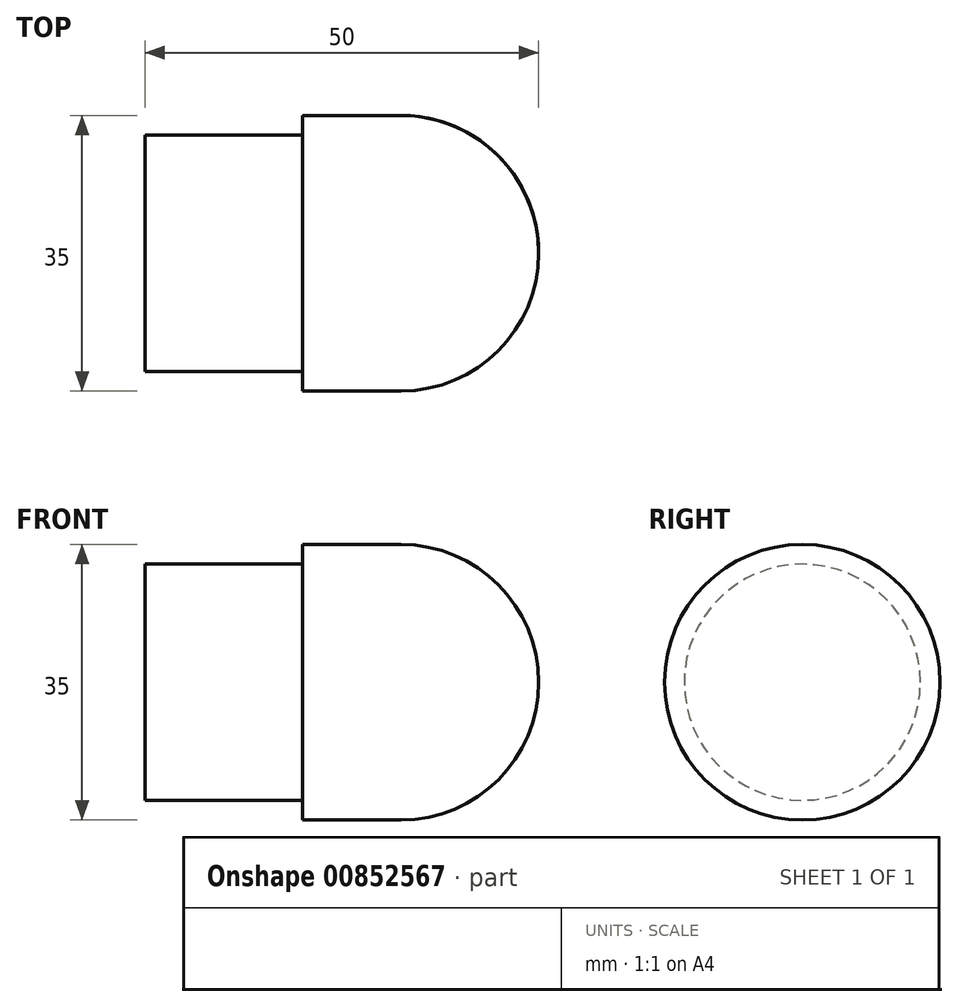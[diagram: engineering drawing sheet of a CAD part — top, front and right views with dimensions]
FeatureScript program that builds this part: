
annotation { "Feature Type Name" : "Feature", "Feature Type Description" : "" }
export const myFeature = defineFeature(function(context is Context, id is Id, definition is map)
    precondition{}
    {
        {
            var Q0;
            Q0=qCreatedBy(makeId("Top.planeOp"),FACE);
            var sketch = newSketch(context, id + "F0", { "sketchPlane" : qUnion([Q0])});
            skLineSegment(sketch, "E0", {"start": v(0, 0) * mm, "end": v(50, 0) * mm});
            skLineSegment(sketch, "E1", {"start": v(50, 0) * mm, "end": v(50, 0) * mm});
            skLineSegment(sketch, "E2", {"start": v(32.5, 17.5) * mm, "end": v(20, 17.5) * mm});
            skLineSegment(sketch, "E3", {"start": v(20, 17.5) * mm, "end": v(20, 15) * mm});
            skLineSegment(sketch, "E4", {"start": v(20, 15) * mm, "end": v(0, 15) * mm});
            skLineSegment(sketch, "E5", {"start": v(0, 15) * mm, "end": v(0, 0) * mm});
            skPoint(sketch, "E6.visualSharp", {"position": v(50, 17.5) * mm});
            skArc(sketch, "E6.filletArc", {"start": v(50, 0) * mm, "mid": v(44.87, 12.37) * mm, "end": v(32.5, 17.5) * mm});
            skLineSegment(sketch, "E7", {"start": v(32.5, 17.5) * mm, "end": v(32.5, 0) * mm});
            skSolve(sketch);
        }
        {
            var Q0;
            Q0 = qSketchRegion(id + "F0", true);
            var Q1;
            Q1=sQuery(id+"F0.wireOp",EDGE,"E0");
            revolve(context, id + "F1", {"surfaceOperationType" : NewSurfaceOperationType.NEW, "entities" : qUnion([Q0]), "axis" : qUnion([Q1]), "revolveType" : RevolveType.FULL});
        }
    });
